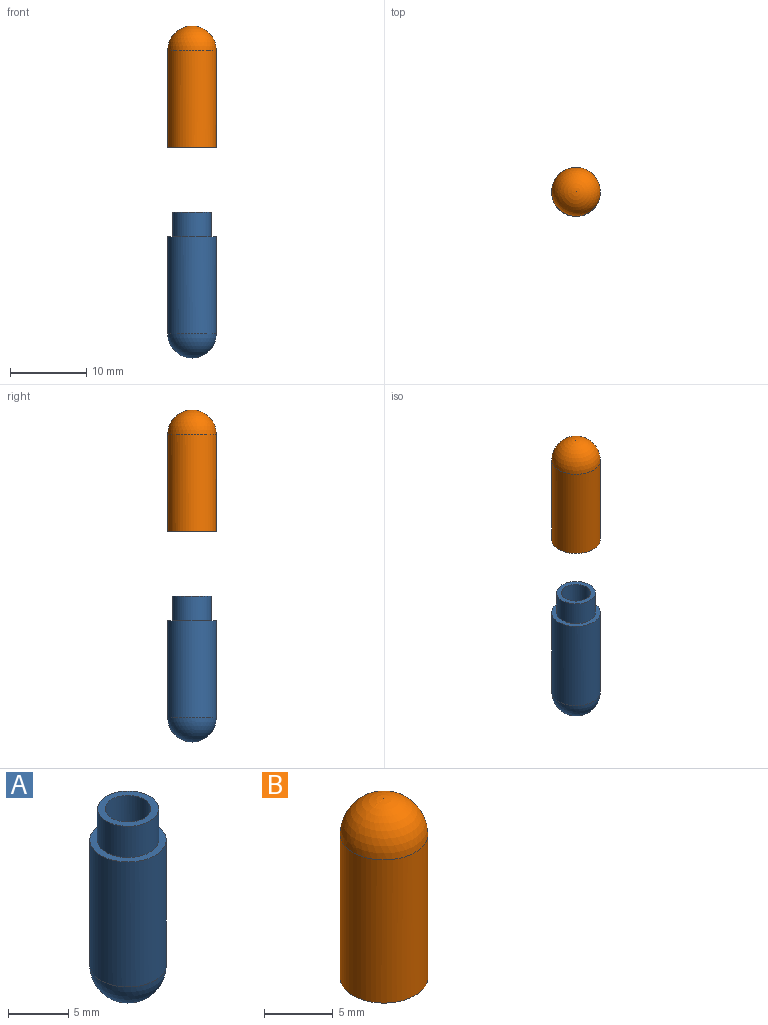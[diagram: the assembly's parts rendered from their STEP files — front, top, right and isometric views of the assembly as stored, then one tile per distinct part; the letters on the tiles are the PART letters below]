
ASSEMBLY  parts=2 mates=1
PART A: 7 faces, bbox 6.4x6.4x19.1 mm
  f0: cylinder r=3.17mm len=12.7mm, axis (0,0,-1), area 253.4mm2, adj f1,f2
  f1: sphere r=3.17mm, area 63.3mm2, adj f0
  f2: plane 6.35x6.35mm, normal (0,0,1), area 11.4mm2, adj f0,f3
  f3: cylinder r=2.54mm len=5.08mm, axis (0,0,-1), area 50.7mm2, adj f2,f4
  f4: plane 5.08x5.08mm, normal (0,0,1), area 8.9mm2, adj f3,f6
  f5: sphere r=1.91mm, area 22.8mm2, adj f6
  f6: cylinder r=1.91mm len=15.88mm, axis (0,0,-1), area 190mm2, adj f4,f5
PART B: 7 faces, bbox 6.4x6.4x15.9 mm
  f0: sphere r=3.17mm, area 63.3mm2, adj f1
  f1: cylinder r=3.17mm len=12.7mm, axis (0,0,-1), area 253.4mm2, adj f0,f2
  f2: plane 6.35x6.35mm, normal (0,0,-1), area 11.4mm2, adj f1,f3
  f3: cylinder r=2.54mm len=5.08mm, axis (0,0,-1), area 50.7mm2, adj f2,f4
  f4: plane 5.08x5.08mm, normal (0,0,-1), area 8.9mm2, adj f3,f6
  f5: sphere r=1.91mm, area 22.8mm2, adj f6
  f6: cylinder r=1.91mm len=9.53mm, axis (0,0,-1), area 114mm2, adj f4,f5
PLACE A t=(0,0,6.35)mm fixed
PLACE B rot(axis=(0,0,1),12.6deg) t=(0,0,18.04)mm
MATE cylindrical B.f1 <-> A.f0  axis (0,0,-1) through (0,0,18.04)mm
